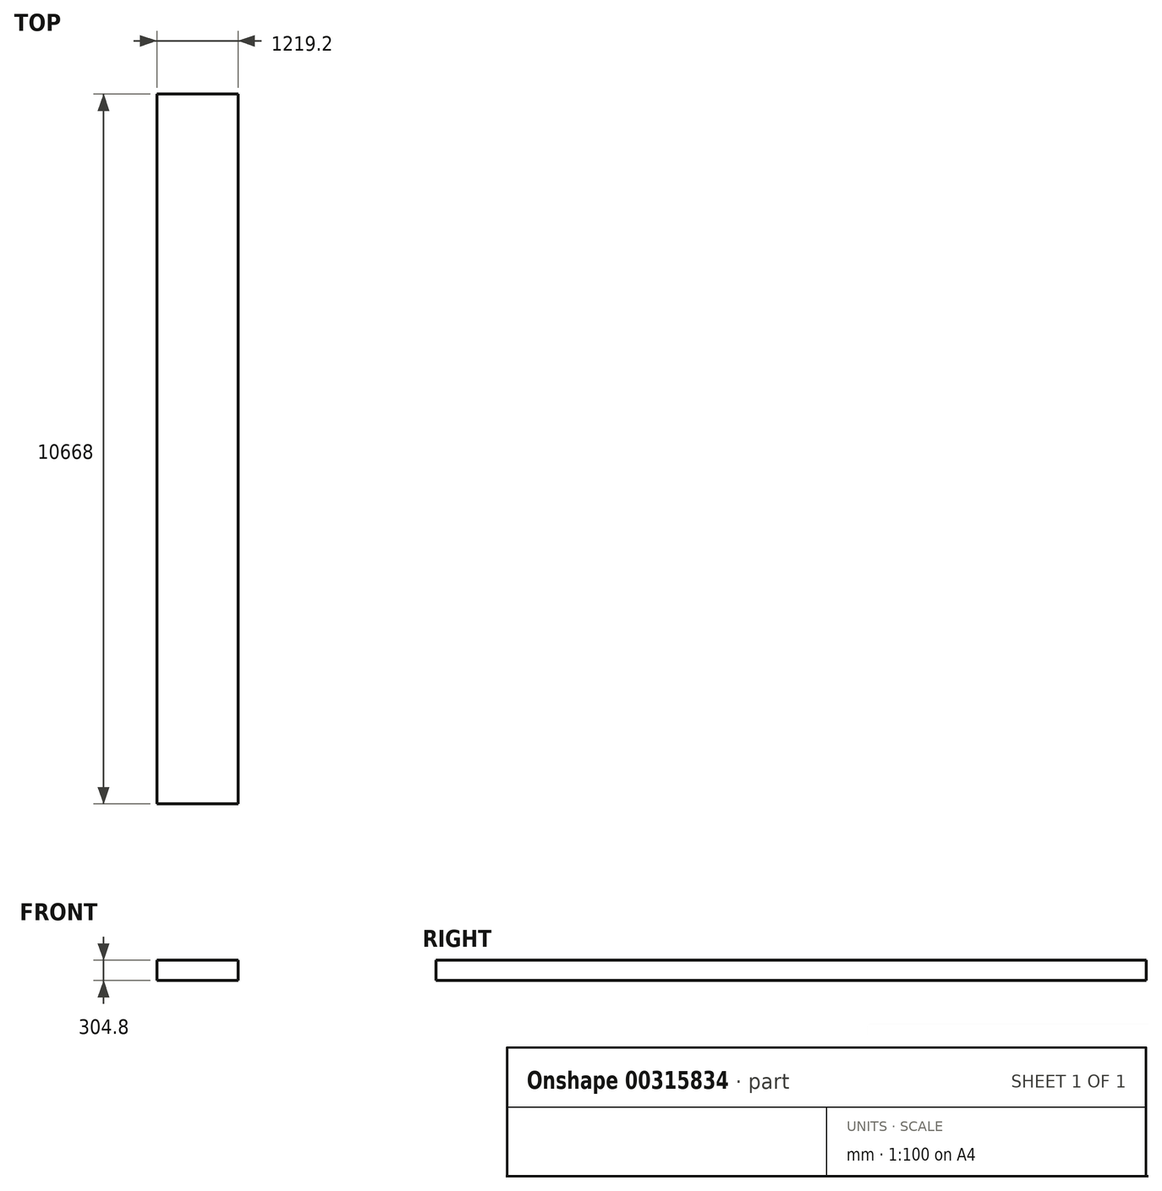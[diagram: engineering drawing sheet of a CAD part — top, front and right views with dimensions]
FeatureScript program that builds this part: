
annotation { "Feature Type Name" : "Feature", "Feature Type Description" : "" }
export const myFeature = defineFeature(function(context is Context, id is Id, definition is map)
    precondition{}
    {
        {
            var Q0;
            Q0=qCreatedBy(makeId("Top.planeOp"),FACE);
            var sketch = newSketch(context, id + "F0", { "sketchPlane" : qUnion([Q0])});
            skLineSegment(sketch, "E0.bottom", {"start": v(-612.14, 9815.66) * mm, "end": v(607.06, 9815.66) * mm});
            skLineSegment(sketch, "E0.top", {"start": v(-612.14, -852.34) * mm, "end": v(607.06, -852.34) * mm});
            skLineSegment(sketch, "E0.left", {"start": v(-612.14, 9815.66) * mm, "end": v(-612.14, -852.34) * mm});
            skLineSegment(sketch, "E0.right", {"start": v(607.06, 9815.66) * mm, "end": v(607.06, -852.34) * mm});
            skSolve(sketch);
        }
        {
            var Q0;
            Q0 = qSketchRegion(id + "F0", true);
            extrude(context, id + "F1", {"entities" : qUnion([Q0]), "depth" : 304.8 * mm});
        }
    });
